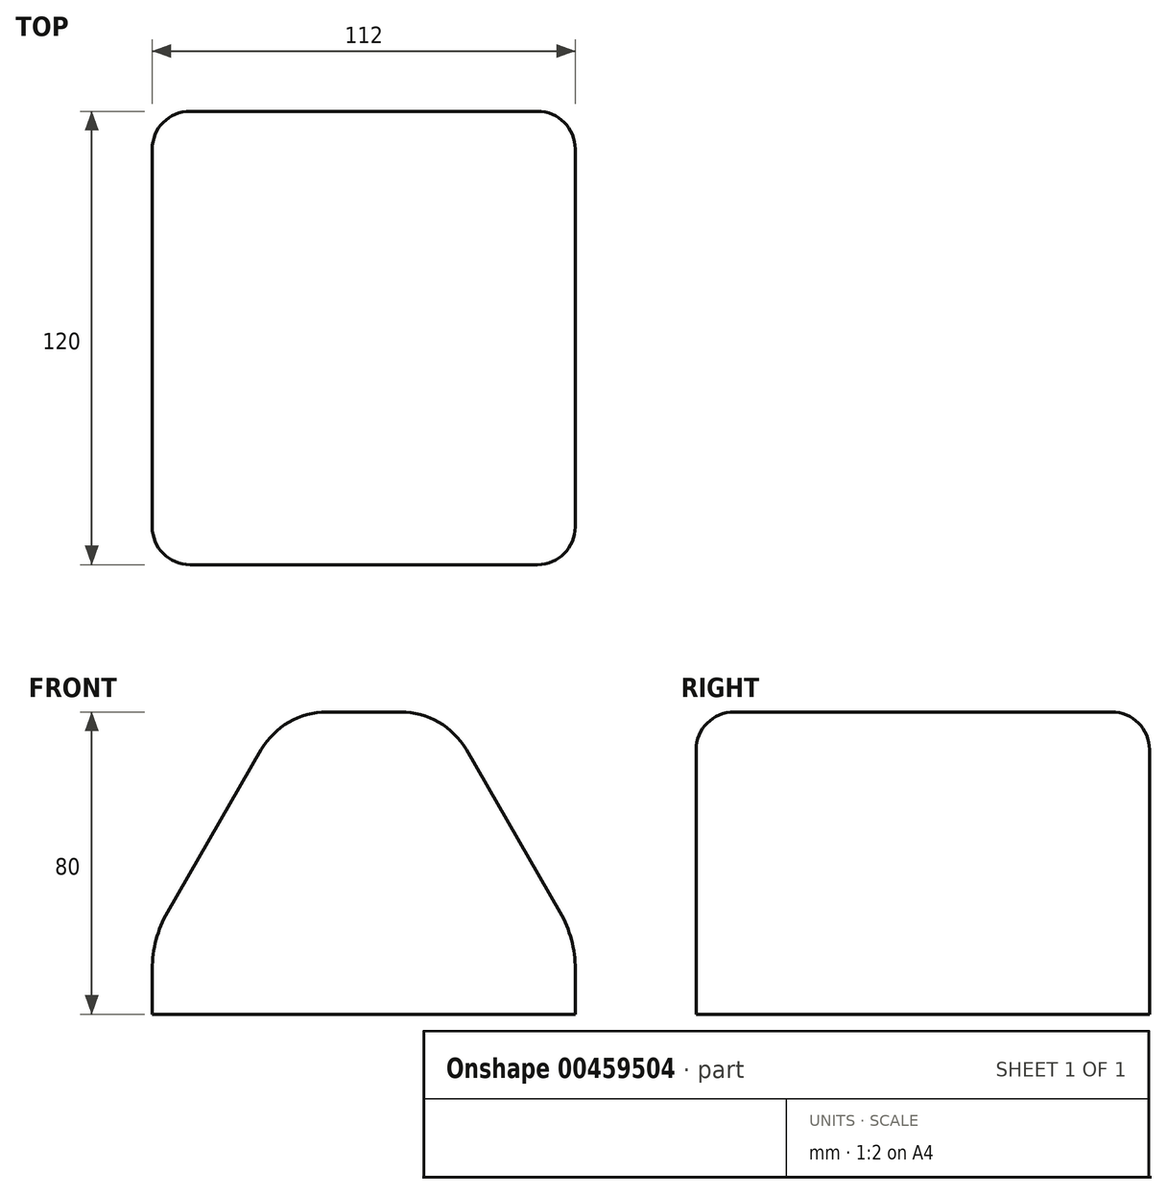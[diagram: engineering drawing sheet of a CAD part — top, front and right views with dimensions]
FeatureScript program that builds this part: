
annotation { "Feature Type Name" : "Feature", "Feature Type Description" : "" }
export const myFeature = defineFeature(function(context is Context, id is Id, definition is map)
    precondition{}
    {
        {
            var Q0;
            Q0=qCreatedBy(makeId("Top.planeOp"),FACE);
            var sketch = newSketch(context, id + "F0", { "sketchPlane" : qUnion([Q0])});
            skLineSegment(sketch, "E0.bottom", {"start": v(-55.98, 25.98) * mm, "end": v(56.02, 25.98) * mm});
            skLineSegment(sketch, "E0.top", {"start": v(-55.98, -94.02) * mm, "end": v(56.02, -94.02) * mm});
            skLineSegment(sketch, "E0.left", {"start": v(-55.98, 25.98) * mm, "end": v(-55.98, -94.02) * mm});
            skLineSegment(sketch, "E0.right", {"start": v(56.02, 25.98) * mm, "end": v(56.02, -94.02) * mm});
            skSolve(sketch);
        }
        {
            var Q0;
            Q0=makeQuery(id+"F0.imprint","IMPRINT",FACE,{"disambiguationData":[TD([[makeQuery(id+"F0.imprint","IMPRINT",EDGE,{"derivedFrom":sQuery(id+"F0.wireOp",EDGE,"E0.bottom")}),-1.0]])]});
            extrude(context, id + "F1", {"entities" : qUnion([Q0]), "depth" : 20 * mm});
        }
        {
            var Q0;
            Q0=makeQuery(id+"F1.opExtrude","CAP_FACE",FACE,{"disambiguationData":[OSD([sQuery(id+"F0.wireOp",EDGE,"E0.bottom"),sQuery(id+"F0.wireOp",EDGE,"E0.top"),sQuery(id+"F0.wireOp",EDGE,"E0.left"),sQuery(id+"F0.wireOp",EDGE,"E0.right")])],"isStart":false});
            extrude(context, id + "F2", {"entities" : qUnion([Q0]), "depth" : 60 * mm});
        }
        {
            var Q0;
            Q0=makeQuery(id+"F2.opExtrude","CAP_EDGE",EDGE,{"disambiguationData":[OSD([sQuery(id+"F0.wireOp",EDGE,"E0.right")])],"isStart":false});
            chamfer(context, id + "F3", {"entities" : qUnion([Q0]), "chamferType" : ChamferType.OFFSET_ANGLE, "width" : 60 * mm, "oppositeDirection" : false, "angle" : 30 * degree, "tangentPropagation" : true});
        }
        {
            var Q0;
            Q0=makeQuery(id+"F2.opExtrude","CAP_EDGE",EDGE,{"disambiguationData":[OSD([sQuery(id+"F0.wireOp",EDGE,"E0.left")])],"isStart":false});
            chamfer(context, id + "F4", {"entities" : qUnion([Q0]), "chamferType" : ChamferType.OFFSET_ANGLE, "width" : 60 * mm, "oppositeDirection" : true, "angle" : 30 * degree, "tangentPropagation" : true});
        }
        {
            var Q0;
            {var subQ0=sQuery(id+"F0.wireOp",EDGE,"E0.right");Q0=makeQuery(id+"F3.opChamfer","BLEND_EDGE",EDGE,{"blendedFrom":[makeQuery(id+"F2.opExtrude","CAP_EDGE",EDGE,{"disambiguationData":[OSD([subQ0])],"isStart":false}),makeQuery(id+"F2.opExtrude","CAP_FACE",FACE,{"disambiguationData":[OSD([sQuery(id+"F0.wireOp",EDGE,"E0.bottom"),sQuery(id+"F0.wireOp",EDGE,"E0.top"),sQuery(id+"F0.wireOp",EDGE,"E0.left"),subQ0])],"isStart":false})],"blendedInto":[makeQuery(id+"F2.opExtrude","CAP_FACE",FACE,{"disambiguationData":[OSD([sQuery(id+"F0.wireOp",EDGE,"E0.bottom"),sQuery(id+"F0.wireOp",EDGE,"E0.top"),sQuery(id+"F0.wireOp",EDGE,"E0.left"),subQ0])],"isStart":false})]});}
            var Q1;
            {var subQ0=sQuery(id+"F0.wireOp",EDGE,"E0.left");Q1=makeQuery(id+"F4.opChamfer","BLEND_EDGE",EDGE,{"blendedFrom":[makeQuery(id+"F2.opExtrude","CAP_EDGE",EDGE,{"disambiguationData":[OSD([subQ0])],"isStart":false}),makeQuery(id+"F2.opExtrude","CAP_FACE",FACE,{"disambiguationData":[OSD([sQuery(id+"F0.wireOp",EDGE,"E0.bottom"),sQuery(id+"F0.wireOp",EDGE,"E0.top"),subQ0,sQuery(id+"F0.wireOp",EDGE,"E0.right")])],"isStart":false})],"blendedInto":[makeQuery(id+"F2.opExtrude","CAP_FACE",FACE,{"disambiguationData":[OSD([sQuery(id+"F0.wireOp",EDGE,"E0.bottom"),sQuery(id+"F0.wireOp",EDGE,"E0.top"),subQ0,sQuery(id+"F0.wireOp",EDGE,"E0.right")])],"isStart":false})]});}
            fillet(context, id + "F5", {"entities" : qUnion([Q0, Q1]), "radius" : 20 * mm, "tangentPropagation" : true, "allowEdgeOverflow" : false});
        }
        {
            var Q0;
            Q0=makeQuery(id+"F1.opExtrude","SWEPT_BODY",BODY,{"disambiguationData":[OSD([sQuery(id+"F0.wireOp",EDGE,"E0.bottom"),sQuery(id+"F0.wireOp",EDGE,"E0.top"),sQuery(id+"F0.wireOp",EDGE,"E0.left"),sQuery(id+"F0.wireOp",EDGE,"E0.right")])]});
            var Q1;
            Q1=makeQuery(id+"F2.opExtrude","SWEPT_BODY",BODY,{"disambiguationData":[OSD([sQuery(id+"F0.wireOp",EDGE,"E0.bottom"),sQuery(id+"F0.wireOp",EDGE,"E0.top"),sQuery(id+"F0.wireOp",EDGE,"E0.left"),sQuery(id+"F0.wireOp",EDGE,"E0.right")])]});
            booleanBodies(context, id + "F6", {"operationType" : BooleanOperationType.UNION, "tools" : qUnion([Q0, Q1])});
        }
        {
            var Q0;
            {var subQ0=sQuery(id+"F0.wireOp",EDGE,"E0.left");Q0=makeQuery(id+"F6.opBoolean","MERGE",EDGE,{"derivedFrom":[makeQuery(id+"F1.opExtrude","CAP_EDGE",EDGE,{"disambiguationData":[OSD([subQ0])],"isStart":false}),makeQuery(id+"F4.opChamfer","BLEND_EDGE",EDGE,{"blendedFrom":[makeQuery(id+"F2.opExtrude","CAP_EDGE",EDGE,{"disambiguationData":[OSD([subQ0])],"isStart":false}),makeQuery(id+"F2.opExtrude","CAP_FACE",FACE,{"disambiguationData":[OSD([sQuery(id+"F0.wireOp",EDGE,"E0.bottom"),sQuery(id+"F0.wireOp",EDGE,"E0.top"),subQ0,sQuery(id+"F0.wireOp",EDGE,"E0.right")])],"isStart":true})],"blendedInto":[makeQuery(id+"F2.opExtrude","CAP_FACE",FACE,{"disambiguationData":[OSD([sQuery(id+"F0.wireOp",EDGE,"E0.bottom"),sQuery(id+"F0.wireOp",EDGE,"E0.top"),subQ0,sQuery(id+"F0.wireOp",EDGE,"E0.right")])],"isStart":true})]})]});}
            var Q1;
            {var subQ0=sQuery(id+"F0.wireOp",EDGE,"E0.right");Q1=makeQuery(id+"F6.opBoolean","MERGE",EDGE,{"derivedFrom":[makeQuery(id+"F1.opExtrude","CAP_EDGE",EDGE,{"disambiguationData":[OSD([subQ0])],"isStart":false}),makeQuery(id+"F3.opChamfer","BLEND_EDGE",EDGE,{"blendedFrom":[makeQuery(id+"F2.opExtrude","CAP_EDGE",EDGE,{"disambiguationData":[OSD([subQ0])],"isStart":false}),makeQuery(id+"F2.opExtrude","CAP_FACE",FACE,{"disambiguationData":[OSD([sQuery(id+"F0.wireOp",EDGE,"E0.bottom"),sQuery(id+"F0.wireOp",EDGE,"E0.top"),sQuery(id+"F0.wireOp",EDGE,"E0.left"),subQ0])],"isStart":true})],"blendedInto":[makeQuery(id+"F2.opExtrude","CAP_FACE",FACE,{"disambiguationData":[OSD([sQuery(id+"F0.wireOp",EDGE,"E0.bottom"),sQuery(id+"F0.wireOp",EDGE,"E0.top"),sQuery(id+"F0.wireOp",EDGE,"E0.left"),subQ0])],"isStart":true})]})]});}
            fillet(context, id + "F7", {"entities" : qUnion([Q0, Q1]), "radius" : 30 * mm, "tangentPropagation" : true, "allowEdgeOverflow" : false});
        }
        {
            var Q0;
            Q0=makeQuery(id+"F4.opChamfer","BLEND_EDGE",EDGE,{"blendedFrom":[makeQuery(id+"F2.opExtrude","CAP_EDGE",EDGE,{"disambiguationData":[OSD([sQuery(id+"F0.wireOp",EDGE,"E0.left")])],"isStart":false}),makeQuery(id+"F2.opExtrude","SWEPT_FACE",FACE,{"disambiguationData":[OSD([sQuery(id+"F0.wireOp",EDGE,"E0.top")])]})],"blendedInto":[makeQuery(id+"F2.opExtrude","SWEPT_FACE",FACE,{"disambiguationData":[OSD([sQuery(id+"F0.wireOp",EDGE,"E0.top")])]})]});
            var Q1;
            Q1=makeQuery(id+"F4.opChamfer","BLEND_EDGE",EDGE,{"blendedFrom":[makeQuery(id+"F2.opExtrude","CAP_EDGE",EDGE,{"disambiguationData":[OSD([sQuery(id+"F0.wireOp",EDGE,"E0.left")])],"isStart":false}),makeQuery(id+"F2.opExtrude","SWEPT_FACE",FACE,{"disambiguationData":[OSD([sQuery(id+"F0.wireOp",EDGE,"E0.bottom")])]})],"blendedInto":[makeQuery(id+"F2.opExtrude","SWEPT_FACE",FACE,{"disambiguationData":[OSD([sQuery(id+"F0.wireOp",EDGE,"E0.bottom")])]})]});
            fillet(context, id + "F8", {"entities" : qUnion([Q0, Q1]), "radius" : 10 * mm, "tangentPropagation" : true, "allowEdgeOverflow" : false});
        }
    });
